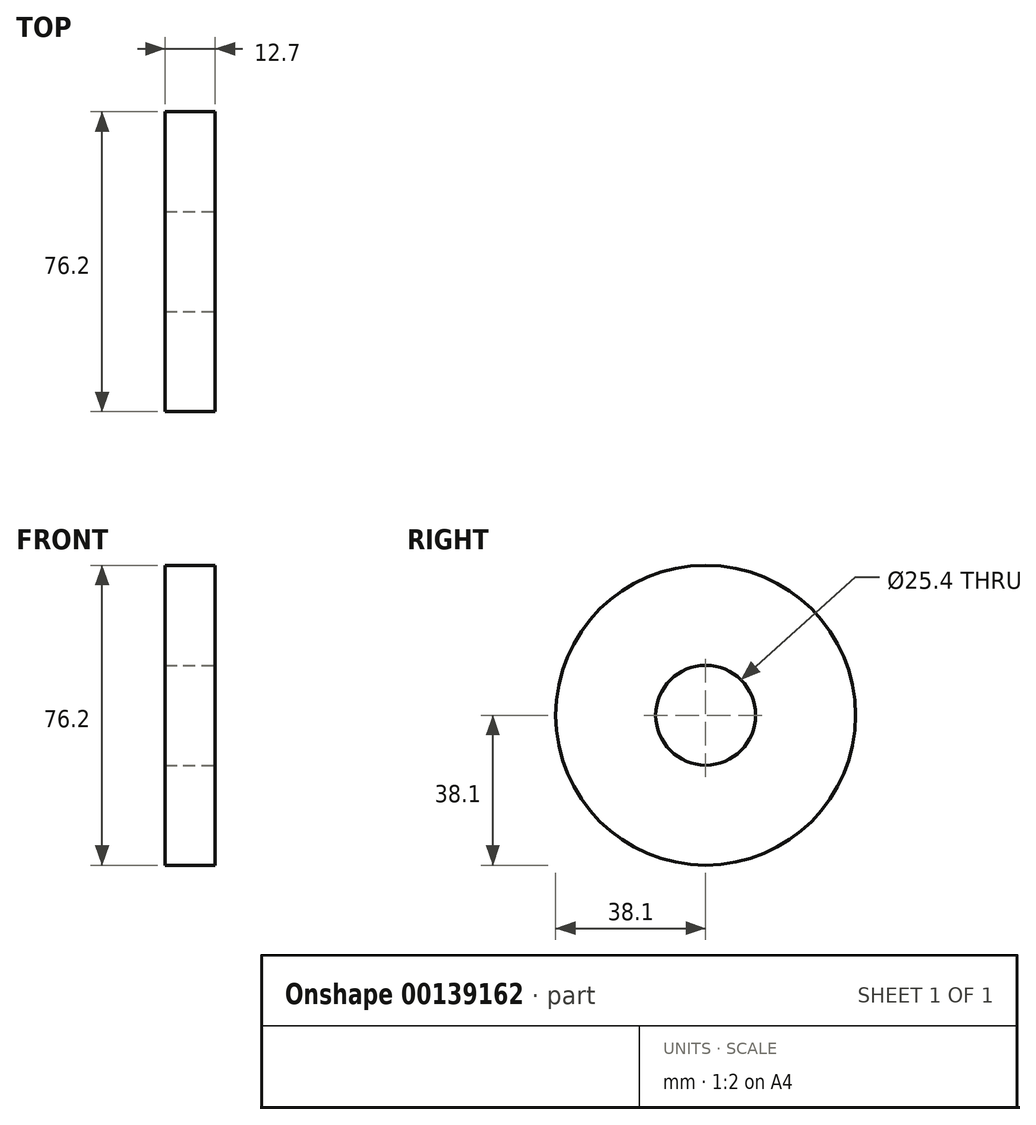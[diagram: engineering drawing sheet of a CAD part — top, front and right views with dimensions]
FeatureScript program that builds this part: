
annotation { "Feature Type Name" : "Feature", "Feature Type Description" : "" }
export const myFeature = defineFeature(function(context is Context, id is Id, definition is map)
    precondition{}
    {
        {
            var Q0;
            Q0=qCreatedBy(makeId("Right.planeOp"),FACE);
            var sketch = newSketch(context, id + "F0", { "sketchPlane" : qUnion([Q0])});
            skCircle(sketch, "E0", {"center": v(0, 0) * mm, "radius": 38.1 * mm});
            skSolve(sketch);
        }
        {
            var Q0;
            Q0 = qSketchRegion(id + "F0", true);
            extrude(context, id + "F1", {"entities" : qUnion([Q0]), "endBound" : BoundingType.SYMMETRIC, "depth" : 12.7 * mm, "hasSecondDirection" : true, "secondDirectionOppositeDirection" : true, "secondDirectionDepth" : 6.35 * mm});
        }
        {
            var Q0;
            Q0=makeQuery(id+"F1.opExtrude","CAP_FACE",FACE,{"disambiguationData":[OSD([sQuery(id+"F0.wireOp",EDGE,"E0")])],"isStart":false});
            var sketch = newSketch(context, id + "F2", { "sketchPlane" : qUnion([Q0])});
            skCircle(sketch, "E1", {"center": v(0, 0) * mm, "radius": 12.7 * mm});
            skSolve(sketch);
        }
        {
            var Q0;
            Q0 = qSketchRegion(id + "F2", true);
            extrude(context, id + "F3", {"entities" : qUnion([Q0]), "operationType" : NewBodyOperationType.REMOVE, "endBound" : BoundingType.THROUGH_ALL, "oppositeDirection" : true, "depth" : 25.4 * mm});
        }
    });
